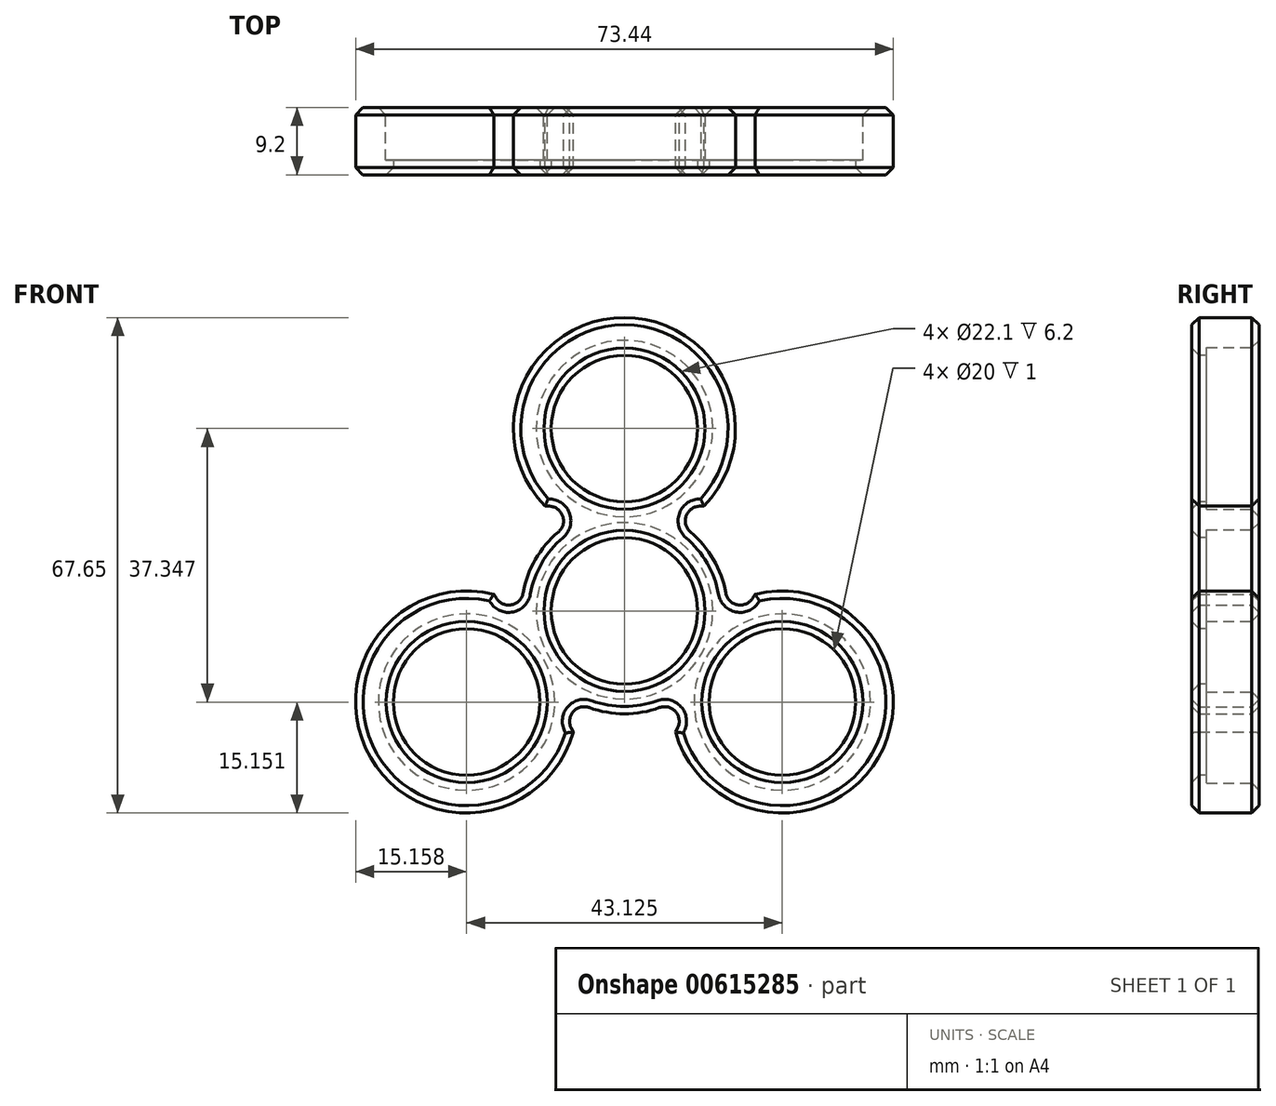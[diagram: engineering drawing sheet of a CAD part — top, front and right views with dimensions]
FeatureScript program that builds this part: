
annotation { "Feature Type Name" : "Feature", "Feature Type Description" : "" }
export const myFeature = defineFeature(function(context is Context, id is Id, definition is map)
    precondition{}
    {
        {
            var Q0;
            Q0=qCreatedBy(makeId("Front.planeOp"),FACE);
            var sketch = newSketch(context, id + "F0", { "sketchPlane" : qUnion([Q0])});
            skCircle(sketch, "E0", {"center": v(0, 0) * mm, "radius": 11.05 * mm});
            skArc(sketch, "E1", {"start": v(-2.48, 13.83) * mm, "mid": v(-12.17, 7.02) * mm, "end": v(-13.22, -4.76) * mm});
            skCircle(sketch, "E2.MirrorC", {"center": v(0, 24.9) * mm, "radius": 11.05 * mm});
            skArc(sketch, "E3.MirrorC", {"start": v(-10.86, 14.33) * mm, "mid": v(0, 40.05) * mm, "end": v(10.86, 14.33) * mm});
            skArc(sketch, "E4.1.0", {"start": v(-6.98, -16.57) * mm, "mid": v(-34.69, -20.03) * mm, "end": v(-17.84, 2.24) * mm});
            skCircle(sketch, "E4.1.1", {"center": v(-21.56, -12.45) * mm, "radius": 11.05 * mm});
            skArc(sketch, "E4.2.0", {"start": v(17.84, 2.24) * mm, "mid": v(34.69, -20.03) * mm, "end": v(6.98, -16.57) * mm});
            skCircle(sketch, "E4.2.1", {"center": v(21.56, -12.45) * mm, "radius": 11.05 * mm});
            skLineSegment(sketch, "E5", {"start": v(-10.86, 14.33) * mm, "end": v(-2.48, 13.83) * mm});
            skLineSegment(sketch, "E6.MirrorCS", {"start": v(10.86, 14.33) * mm, "end": v(2.48, 13.83) * mm});
            skLineSegment(sketch, "E7.1.0", {"start": v(-6.98, -16.57) * mm, "end": v(-10.73, -9.06) * mm});
            skLineSegment(sketch, "E7.1.1", {"start": v(-17.84, 2.24) * mm, "end": v(-13.22, -4.76) * mm});
            skLineSegment(sketch, "E7.2.0", {"start": v(17.84, 2.24) * mm, "end": v(13.22, -4.76) * mm});
            skLineSegment(sketch, "E7.2.1", {"start": v(6.98, -16.57) * mm, "end": v(10.73, -9.06) * mm});
            skArc(sketch, "E8.trimOffspring", {"start": v(13.22, -4.76) * mm, "mid": v(12.17, 7.03) * mm, "end": v(2.48, 13.83) * mm});
            skArc(sketch, "E9.trimOffspring", {"start": v(-10.73, -9.06) * mm, "mid": v(0, -14.05) * mm, "end": v(10.73, -9.06) * mm});
            skSolve(sketch);
        }
        {
            var Q0;
            Q0 = qSketchRegion(id + "F0", true);
            extrude(context, id + "F1", {"entities" : qUnion([Q0]), "depth" : 9.2 * mm, "offsetDistance" : 25 * mm});
        }
        {
            var Q0;
            Q0=makeQuery(id+"F1.opExtrude","CAP_FACE",FACE,{"disambiguationData":[OSD([sQuery(id+"F0.wireOp",EDGE,"E0"),sQuery(id+"F0.wireOp",EDGE,"E1"),sQuery(id+"F0.wireOp",EDGE,"E2.MirrorC"),sQuery(id+"F0.wireOp",EDGE,"E3.MirrorC"),sQuery(id+"F0.wireOp",EDGE,"E4.1.0"),sQuery(id+"F0.wireOp",EDGE,"E4.1.1"),sQuery(id+"F0.wireOp",EDGE,"E4.2.0"),sQuery(id+"F0.wireOp",EDGE,"E4.2.1"),sQuery(id+"F0.wireOp",EDGE,"E5"),sQuery(id+"F0.wireOp",EDGE,"E6.MirrorCS"),sQuery(id+"F0.wireOp",EDGE,"E7.1.0"),sQuery(id+"F0.wireOp",EDGE,"E7.1.1"),sQuery(id+"F0.wireOp",EDGE,"E7.2.0"),sQuery(id+"F0.wireOp",EDGE,"E7.2.1"),sQuery(id+"F0.wireOp",EDGE,"E8.trimOffspring"),sQuery(id+"F0.wireOp",EDGE,"E9.trimOffspring")])],"isStart":false});
            var sketch = newSketch(context, id + "F2", { "sketchPlane" : qUnion([Q0])});
            skCircle(sketch, "E10", {"center": v(0, 24.9) * mm, "radius": 11.05 * mm});
            skCircle(sketch, "E11.1.0", {"center": v(-21.56, -12.45) * mm, "radius": 11.05 * mm});
            skCircle(sketch, "E11.2.0", {"center": v(21.56, -12.45) * mm, "radius": 11.05 * mm});
            skPoint(sketch, "E11.center", {"position": v(0, 0) * mm});
            skCircle(sketch, "E12", {"center": v(0, 24.9) * mm, "radius": 10 * mm});
            skCircle(sketch, "E13.1.0", {"center": v(-21.56, -12.45) * mm, "radius": 10 * mm});
            skCircle(sketch, "E13.2.0", {"center": v(21.56, -12.45) * mm, "radius": 10 * mm});
            skCircle(sketch, "E14", {"center": v(0, 0) * mm, "radius": 11.05 * mm});
            skCircle(sketch, "E15", {"center": v(0, 0) * mm, "radius": 10 * mm});
            skSolve(sketch);
        }
        {
            var Q0;
            Q0 = qSketchRegion(id + "F2", true);
            extrude(context, id + "F3", {"entities" : qUnion([Q0]), "operationType" : NewBodyOperationType.ADD, "oppositeDirection" : true, "depth" : 2 * mm, "offsetDistance" : 25 * mm});
        }
        {
            var Q0;
            Q0=makeQuery(id+"F1.opExtrude","SWEPT_EDGE",EDGE,{"disambiguationData":[OSD([sQuery(id+"F0.wireOp",EDGE,"E6.MirrorCS"),sQuery(id+"F0.wireOp",EDGE,"E8.trimOffspring")])]});
            var Q1;
            Q1=makeQuery(id+"F1.opExtrude","SWEPT_EDGE",EDGE,{"disambiguationData":[OSD([sQuery(id+"F0.wireOp",EDGE,"E1"),sQuery(id+"F0.wireOp",EDGE,"E5")])]});
            var Q2;
            Q2=makeQuery(id+"F1.opExtrude","SWEPT_EDGE",EDGE,{"disambiguationData":[OSD([sQuery(id+"F0.wireOp",EDGE,"E1"),sQuery(id+"F0.wireOp",EDGE,"E7.1.1")])]});
            var Q3;
            Q3=makeQuery(id+"F1.opExtrude","SWEPT_EDGE",EDGE,{"disambiguationData":[OSD([sQuery(id+"F0.wireOp",EDGE,"E7.1.0"),sQuery(id+"F0.wireOp",EDGE,"E9.trimOffspring")])]});
            var Q4;
            Q4=makeQuery(id+"F1.opExtrude","SWEPT_EDGE",EDGE,{"disambiguationData":[OSD([sQuery(id+"F0.wireOp",EDGE,"E7.2.1"),sQuery(id+"F0.wireOp",EDGE,"E9.trimOffspring")])]});
            var Q5;
            Q5=makeQuery(id+"F1.opExtrude","SWEPT_EDGE",EDGE,{"disambiguationData":[OSD([sQuery(id+"F0.wireOp",EDGE,"E7.2.0"),sQuery(id+"F0.wireOp",EDGE,"E8.trimOffspring")])]});
            fillet(context, id + "F4", {"entities" : qUnion([Q0, Q1, Q2, Q3, Q4, Q5]), "radius" : 2 * mm, "tangentPropagation" : true, "allowEdgeOverflow" : false});
        }
        {
            var Q0;
            Q0=makeQuery(id+"F1.opExtrude","CAP_FACE",FACE,{"disambiguationData":[OSD([sQuery(id+"F0.wireOp",EDGE,"E0"),sQuery(id+"F0.wireOp",EDGE,"E1"),sQuery(id+"F0.wireOp",EDGE,"E2.MirrorC"),sQuery(id+"F0.wireOp",EDGE,"E3.MirrorC"),sQuery(id+"F0.wireOp",EDGE,"E4.1.0"),sQuery(id+"F0.wireOp",EDGE,"E4.1.1"),sQuery(id+"F0.wireOp",EDGE,"E4.2.0"),sQuery(id+"F0.wireOp",EDGE,"E4.2.1"),sQuery(id+"F0.wireOp",EDGE,"E5"),sQuery(id+"F0.wireOp",EDGE,"E6.MirrorCS"),sQuery(id+"F0.wireOp",EDGE,"E7.1.0"),sQuery(id+"F0.wireOp",EDGE,"E7.1.1"),sQuery(id+"F0.wireOp",EDGE,"E7.2.0"),sQuery(id+"F0.wireOp",EDGE,"E7.2.1"),sQuery(id+"F0.wireOp",EDGE,"E8.trimOffspring"),sQuery(id+"F0.wireOp",EDGE,"E9.trimOffspring")])],"isStart":false});
            var sketch = newSketch(context, id + "F5", { "sketchPlane" : qUnion([Q0])});
            skArc(sketch, "E16", {"start": v(1.77, 21.17) * mm, "mid": v(0, 24.92) * mm, "end": v(-1.77, 21.17) * mm});
            skLineSegment(sketch, "E17", {"start": v(-1.77, 21.17) * mm, "end": v(0, 18.91) * mm});
            skLineSegment(sketch, "E18", {"start": v(1.77, 21.17) * mm, "end": v(0, 18.91) * mm});
            skPoint(sketch, "E19.orphan", {"position": v(1.84, 21.27) * mm});
            skPoint(sketch, "E20.orphan", {"position": v(-1.84, 21.27) * mm});
            skArc(sketch, "E21.1.0", {"start": v(-19.22, -9.06) * mm, "mid": v(-21.58, -12.46) * mm, "end": v(-17.45, -12.12) * mm});
            skLineSegment(sketch, "E21.1.1", {"start": v(-17.45, -12.12) * mm, "end": v(-16.38, -9.46) * mm});
            skLineSegment(sketch, "E21.1.2", {"start": v(-19.22, -9.06) * mm, "end": v(-16.38, -9.46) * mm});
            skArc(sketch, "E21.2.0", {"start": v(17.45, -12.12) * mm, "mid": v(21.58, -12.46) * mm, "end": v(19.22, -9.06) * mm});
            skLineSegment(sketch, "E21.2.1", {"start": v(19.22, -9.06) * mm, "end": v(16.38, -9.46) * mm});
            skLineSegment(sketch, "E21.2.2", {"start": v(17.45, -12.12) * mm, "end": v(16.38, -9.46) * mm});
            skPoint(sketch, "E21.center", {"position": v(0, 0) * mm});
            skSolve(sketch);
        }
        {
            var Q0;
            Q0 = qSketchRegion(id + "F5", true);
            extrude(context, id + "F6", {"entities" : qUnion([Q0]), "operationType" : NewBodyOperationType.REMOVE, "oppositeDirection" : true, "depth" : 25 * mm, "offsetDistance" : 25 * mm});
        }
        {
            var Q0;
            Q0=makeQuery(id+"F1.opExtrude","CAP_FACE",FACE,{"disambiguationData":[OSD([sQuery(id+"F0.wireOp",EDGE,"E0"),sQuery(id+"F0.wireOp",EDGE,"E1"),sQuery(id+"F0.wireOp",EDGE,"E2.MirrorC"),sQuery(id+"F0.wireOp",EDGE,"E3.MirrorC"),sQuery(id+"F0.wireOp",EDGE,"E4.1.0"),sQuery(id+"F0.wireOp",EDGE,"E4.1.1"),sQuery(id+"F0.wireOp",EDGE,"E4.2.0"),sQuery(id+"F0.wireOp",EDGE,"E4.2.1"),sQuery(id+"F0.wireOp",EDGE,"E5"),sQuery(id+"F0.wireOp",EDGE,"E6.MirrorCS"),sQuery(id+"F0.wireOp",EDGE,"E7.1.0"),sQuery(id+"F0.wireOp",EDGE,"E7.1.1"),sQuery(id+"F0.wireOp",EDGE,"E7.2.0"),sQuery(id+"F0.wireOp",EDGE,"E7.2.1"),sQuery(id+"F0.wireOp",EDGE,"E8.trimOffspring"),sQuery(id+"F0.wireOp",EDGE,"E9.trimOffspring")])],"isStart":true});
            chamfer(context, id + "F7", {"entities" : qUnion([Q0]), "width" : 1 * mm, "tangentPropagation" : true});
        }
        {
            var Q0;
            Q0=makeQuery(id+"F3.boolean.opBoolean","MERGE",FACE,{"derivedFrom":[makeQuery(id+"F1.opExtrude","CAP_FACE",FACE,{"disambiguationData":[OSD([sQuery(id+"F0.wireOp",EDGE,"E0"),sQuery(id+"F0.wireOp",EDGE,"E1"),sQuery(id+"F0.wireOp",EDGE,"E2.MirrorC"),sQuery(id+"F0.wireOp",EDGE,"E3.MirrorC"),sQuery(id+"F0.wireOp",EDGE,"E4.1.0"),sQuery(id+"F0.wireOp",EDGE,"E4.1.1"),sQuery(id+"F0.wireOp",EDGE,"E4.2.0"),sQuery(id+"F0.wireOp",EDGE,"E4.2.1"),sQuery(id+"F0.wireOp",EDGE,"E5"),sQuery(id+"F0.wireOp",EDGE,"E6.MirrorCS"),sQuery(id+"F0.wireOp",EDGE,"E7.1.0"),sQuery(id+"F0.wireOp",EDGE,"E7.1.1"),sQuery(id+"F0.wireOp",EDGE,"E7.2.0"),sQuery(id+"F0.wireOp",EDGE,"E7.2.1"),sQuery(id+"F0.wireOp",EDGE,"E8.trimOffspring"),sQuery(id+"F0.wireOp",EDGE,"E9.trimOffspring")])],"isStart":false}),makeQuery(id+"F3.opExtrude","CAP_FACE",FACE,{"disambiguationData":[OSD([sQuery(id+"F2.wireOp",EDGE,"E10"),sQuery(id+"F2.wireOp",EDGE,"E12")])],"isStart":true}),makeQuery(id+"F3.opExtrude","CAP_FACE",FACE,{"disambiguationData":[OSD([sQuery(id+"F2.wireOp",EDGE,"E11.1.0"),sQuery(id+"F2.wireOp",EDGE,"E13.1.0")])],"isStart":true}),makeQuery(id+"F3.opExtrude","CAP_FACE",FACE,{"disambiguationData":[OSD([sQuery(id+"F2.wireOp",EDGE,"E11.2.0"),sQuery(id+"F2.wireOp",EDGE,"E13.2.0")])],"isStart":true}),makeQuery(id+"F3.opExtrude","CAP_FACE",FACE,{"disambiguationData":[OSD([sQuery(id+"F2.wireOp",EDGE,"E14"),sQuery(id+"F2.wireOp",EDGE,"E15")])],"isStart":true})]});
            chamfer(context, id + "F8", {"entities" : qUnion([Q0]), "width" : 1 * mm, "tangentPropagation" : true});
        }
    });
